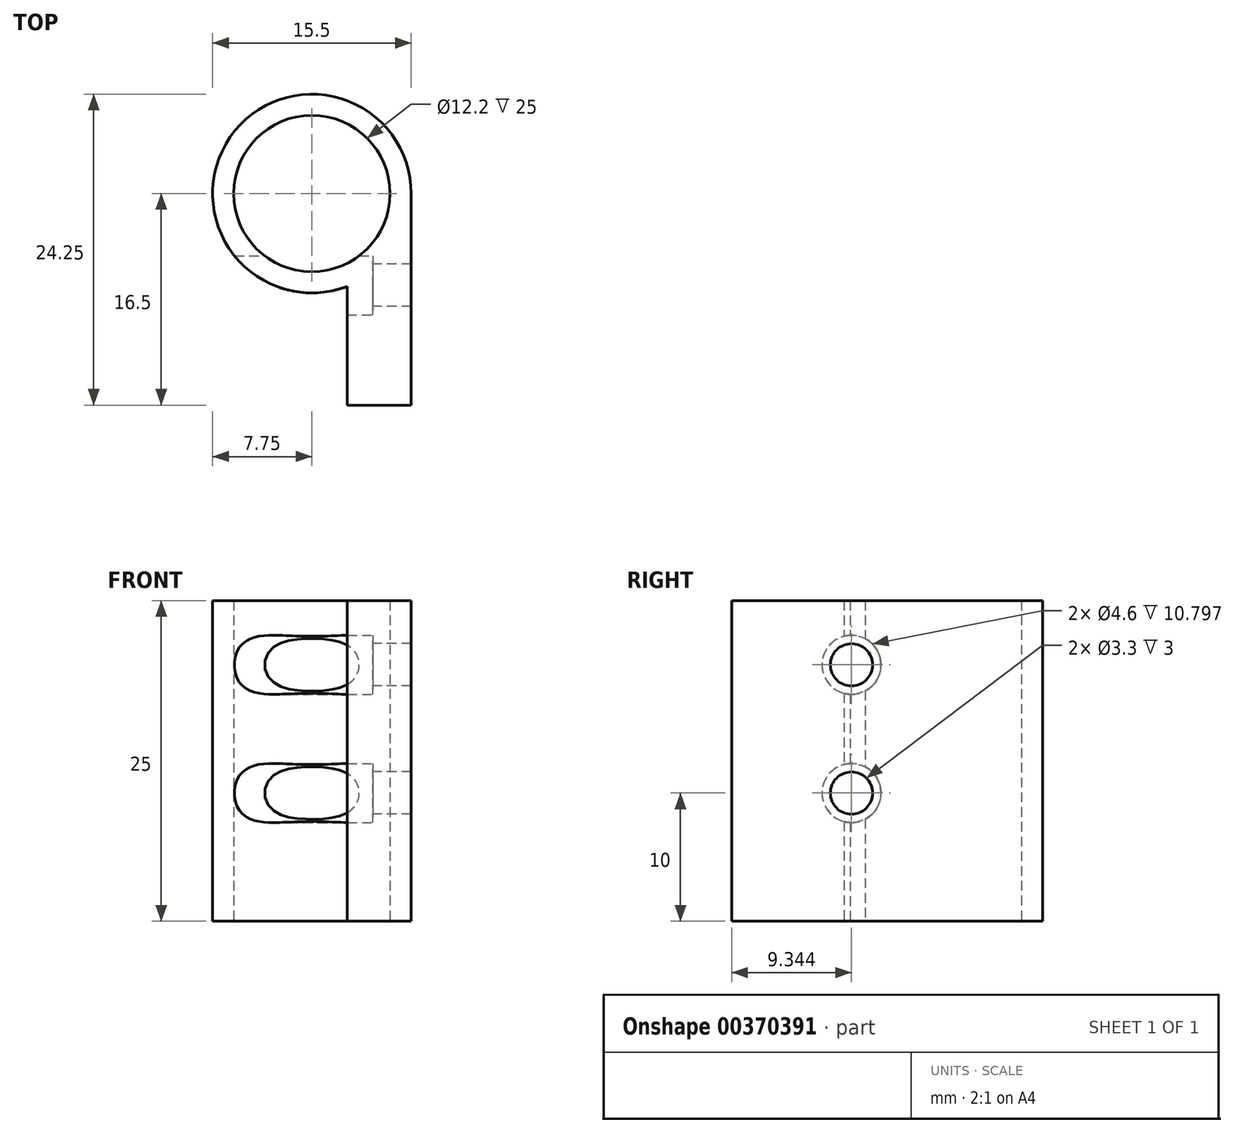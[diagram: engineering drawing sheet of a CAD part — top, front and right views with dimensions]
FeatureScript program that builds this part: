
annotation { "Feature Type Name" : "Feature", "Feature Type Description" : "" }
export const myFeature = defineFeature(function(context is Context, id is Id, definition is map)
    precondition{}
    {
        {
            var Q0;
            Q0=qCreatedBy(makeId("Top.planeOp"),FACE);
            var sketch = newSketch(context, id + "F0", { "sketchPlane" : qUnion([Q0])});
            skLineSegment(sketch, "E0.right", {"start": v(0, 0) * mm, "end": v(0, 0) * mm});
            skCircle(sketch, "E1", {"center": v(0, 0) * mm, "radius": 6.1 * mm});
            skCircle(sketch, "E2", {"center": v(0, 0) * mm, "radius": 7.75 * mm});
            skLineSegment(sketch, "E3.MirrorCS", {"start": v(7.75, 0) * mm, "end": v(7.75, -16.5) * mm});
            skLineSegment(sketch, "E4.MirrorCS", {"start": v(2.75, -16.5) * mm, "end": v(2.75, -7.25) * mm});
            skLineSegment(sketch, "E5.MirrorCS", {"start": v(7.75, -16.5) * mm, "end": v(2.75, -16.5) * mm});
            skLineSegment(sketch, "E6", {"start": v(-8.56, 0) * mm, "end": v(8.94, 0) * mm, "construction": true});
            skPoint(sketch, "E7", {"position": v(7.75, 0) * mm});
            skSolve(sketch);
        }
        {
            var Q0;
            Q0=qSketchRegion(id+"F0",true);
            extrude(context, id + "F1", {"entities" : qUnion([Q0]), "depth" : 25 * mm});
        }
        {
            var Q0;
            Q0=makeQuery(id+"F1.opExtrude","SWEPT_FACE",FACE,{"disambiguationData":[OSD([sQuery(id+"F0.wireOp",EDGE,"E4.MirrorCS")])]});
            var sketch = newSketch(context, id + "F2", { "sketchPlane" : qUnion([Q0])});
            skLineSegment(sketch, "E8", {"start": v(7.16, 25) * mm, "end": v(7.16, 0) * mm, "construction": true});
            skLineSegment(sketch, "E9", {"start": v(16.5, 10) * mm, "end": v(7.25, 10) * mm, "construction": true});
            skLineSegment(sketch, "E10", {"start": v(16.5, 20) * mm, "end": v(7.25, 20) * mm, "construction": true});
            skLineSegment(sketch, "E11", {"start": v(-7.84, 24.99) * mm, "end": v(-7.84, 12.7) * mm, "construction": true});
            skPoint(sketch, "E12", {"position": v(7.16, 20) * mm});
            skPoint(sketch, "E13", {"position": v(7.16, 10) * mm});
            skCircle(sketch, "E14", {"center": v(7.16, 20) * mm, "radius": 2.3 * mm});
            skCircle(sketch, "E15", {"center": v(7.16, 10) * mm, "radius": 2.3 * mm});
            skSolve(sketch);
        }
        {
            var Q0;
            {var subQ0=sQuery(id+"F2.wireOp",EDGE,"E14");var subQ1=makeQuery(id+"F1.opExtrude","SWEPT_EDGE",EDGE,{"disambiguationData":[OSD([sQuery(id+"F0.wireOp",EDGE,"E2"),sQuery(id+"F0.wireOp",EDGE,"E4.MirrorCS")])]});var subQ2=makeQuery(id+"F2.imprint","INTERSECT",VERTEX,{"disambiguationData":[OD(0.0)],"derivedFrom":[subQ1,subQ0]});Q0=makeQuery(id+"F2.imprint","IMPRINT",FACE,{"disambiguationData":[TD([[makeQuery(id+"F2.imprint","IMPRINT",EDGE,{"disambiguationData":[TD([[subQ2,1.0]])],"derivedFrom":subQ0}),1.0]])]});}
            var Q1;
            Q1=qSketchRegion(id+"F2",true);
            extrude(context, id + "F3", {"entities" : qUnion([Q0, Q1]), "operationType" : NewBodyOperationType.REMOVE, "depth" : 25 * mm});
        }
        {
            var Q0;
            Q0=qSketchRegion(id+"F2",true);
            extrude(context, id + "F4", {"entities" : qUnion([Q0]), "operationType" : NewBodyOperationType.REMOVE, "oppositeDirection" : true, "depth" : 2 * mm});
        }
        {
            var Q0;
            Q0=sQuery(id+"F2.wireOp",VERTEX,"E13");
            var Q1;
            Q1=sQuery(id+"F2.wireOp",VERTEX,"E12");
            var Q2;
            Q2=makeQuery(id+"F1.opExtrude","SWEPT_BODY",BODY,{"disambiguationData":[OSD([sQuery(id+"F0.wireOp",EDGE,"E1"),sQuery(id+"F0.wireOp",EDGE,"E2"),sQuery(id+"F0.wireOp",EDGE,"E3.MirrorCS"),sQuery(id+"F0.wireOp",EDGE,"E4.MirrorCS"),sQuery(id+"F0.wireOp",EDGE,"E5.MirrorCS")])]});
            hole(context, id + "F5", {"style" : HoleStyle.SIMPLE, "endStyle" : HoleEndStyle.THROUGH, "standardTappedOrClearance" : lookupTablePath({ "standard" : "ISO", "fit" : "Normal", "size" : "M3", "type" : "Clearance" }), "standardBlindInLast" : lookupTablePath({ "fit" : "Standard", "standard" : "ISO", "size" : "M3", "type" : "Clearance" }), "holeDiameter" : 3.3 * mm, "tappedDepth" : 12 * mm, "tapClearance" : 3, "locations" : qUnion([Q0, Q1]), "scope" : qUnion([Q2])});
        }
    });
